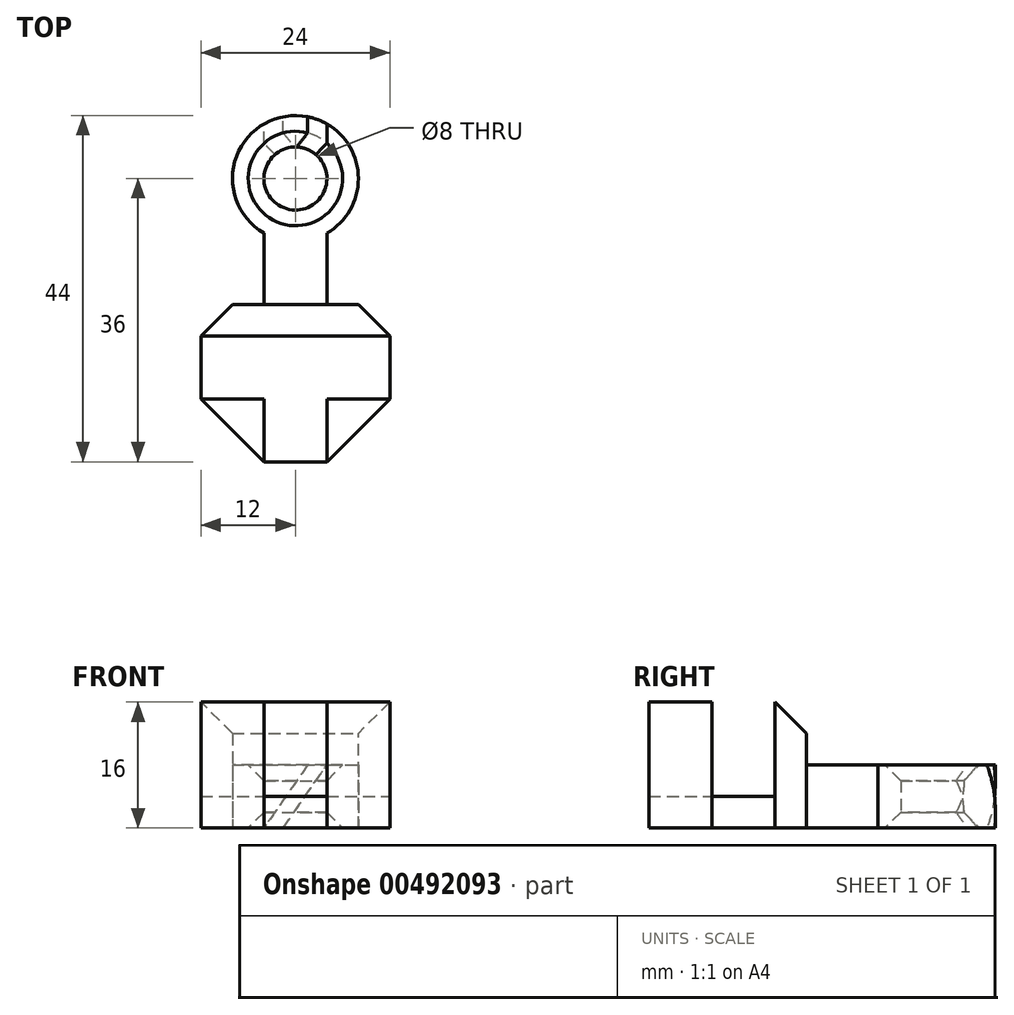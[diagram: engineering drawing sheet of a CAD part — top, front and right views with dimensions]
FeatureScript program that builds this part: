
annotation { "Feature Type Name" : "Feature", "Feature Type Description" : "" }
export const myFeature = defineFeature(function(context is Context, id is Id, definition is map)
    precondition{}
    {
        {
            var Q0;
            Q0=qCreatedBy(makeId("Top.planeOp"),FACE);
            var sketch = newSketch(context, id + "F0", { "sketchPlane" : qUnion([Q0])});
            skLineSegment(sketch, "E0.bottom", {"start": v(16, 4) * mm, "end": v(-16, 4) * mm});
            skLineSegment(sketch, "E0.top", {"start": v(16, -4) * mm, "end": v(-16, -4) * mm});
            skLineSegment(sketch, "E0.left", {"start": v(16, 4) * mm, "end": v(16, -4) * mm});
            skLineSegment(sketch, "E0.right", {"start": v(-16, 4) * mm, "end": v(-16, -4) * mm});
            skPoint(sketch, "E0.middle", {"position": v(0, 0) * mm});
            skLineSegment(sketch, "E1.bottom", {"start": v(-4, -4) * mm, "end": v(4, -4) * mm});
            skLineSegment(sketch, "E1.top", {"start": v(-4, -16) * mm, "end": v(4, -16) * mm});
            skLineSegment(sketch, "E1.left", {"start": v(-4, -4) * mm, "end": v(-4, -16) * mm});
            skLineSegment(sketch, "E1.right", {"start": v(4, -4) * mm, "end": v(4, -16) * mm});
            skLineSegment(sketch, "E2", {"start": v(-16, -4) * mm, "end": v(-16, -8) * mm});
            skLineSegment(sketch, "E3", {"start": v(-16, -8) * mm, "end": v(-8, -8) * mm});
            skLineSegment(sketch, "E4", {"start": v(-8, -8) * mm, "end": v(-8, -16) * mm});
            skLineSegment(sketch, "E5", {"start": v(-8, -16) * mm, "end": v(-4, -16) * mm});
            skLineSegment(sketch, "E6", {"start": v(-16, 4) * mm, "end": v(-16, 8) * mm});
            skLineSegment(sketch, "E7", {"start": v(-16, 8) * mm, "end": v(16, 8) * mm});
            skLineSegment(sketch, "E8", {"start": v(16, 8) * mm, "end": v(16, 4) * mm});
            skLineSegment(sketch, "E9", {"start": v(16, -4) * mm, "end": v(16, -8) * mm});
            skLineSegment(sketch, "E10", {"start": v(16, -8) * mm, "end": v(8, -8) * mm});
            skLineSegment(sketch, "E11", {"start": v(8, -8) * mm, "end": v(8, -16) * mm});
            skLineSegment(sketch, "E12", {"start": v(8, -16) * mm, "end": v(4, -16) * mm});
            skSolve(sketch);
        }
        {
            var Q0;
            Q0 = qSketchRegion(id + "F0", true);
            extrude(context, id + "F1", {"entities" : qUnion([Q0]), "depth" : 4 * mm});
        }
        {
            var Q0;
            {var subQ1=sQuery(id+"F0.wireOp",EDGE,"E1.left");Q0=makeQuery(id+"F0.imprint","IMPRINT",FACE,{"disambiguationData":[TD([[makeQuery(id+"F0.imprint","IMPRINT",EDGE,{"derivedFrom":subQ1}),-1.0]])]});}
            var Q1;
            {var subQ0=sQuery(id+"F0.wireOp",EDGE,"E1.right");Q1=makeQuery(id+"F0.imprint","IMPRINT",FACE,{"disambiguationData":[TD([[makeQuery(id+"F0.imprint","IMPRINT",EDGE,{"derivedFrom":subQ0}),1.0]])]});}
            var Q2;
            Q2=makeQuery(id+"F0.imprint","IMPRINT",FACE,{"disambiguationData":[TD([[makeQuery(id+"F0.imprint","IMPRINT",EDGE,{"derivedFrom":sQuery(id+"F0.wireOp",EDGE,"E0.bottom")}),-1.0]])]});
            extrude(context, id + "F2", {"entities" : qUnion([Q0, Q1, Q2]), "operationType" : NewBodyOperationType.ADD, "depth" : 16 * mm});
        }
        {
            var Q0;
            Q0=qCreatedBy(makeId("Top.planeOp"),FACE);
            var sketch = newSketch(context, id + "F3", { "sketchPlane" : qUnion([Q0])});
            skCircle(sketch, "E13", {"center": v(0, 24) * mm, "radius": 4 * mm});
            skCircle(sketch, "E14", {"center": v(0, 24) * mm, "radius": 8 * mm});
            skLineSegment(sketch, "E15.bottom", {"start": v(4, 17.07) * mm, "end": v(-4, 17.07) * mm, "construction": true});
            skLineSegment(sketch, "E15.top", {"start": v(4, 8) * mm, "end": v(-4, 8) * mm});
            skLineSegment(sketch, "E15.left", {"start": v(4, 17.07) * mm, "end": v(4, 8) * mm});
            skLineSegment(sketch, "E15.right", {"start": v(-4, 17.07) * mm, "end": v(-4, 8) * mm});
            skPoint(sketch, "E15.middle", {"position": v(0, 12.54) * mm});
            skPoint(sketch, "E16", {"position": v(0, 32) * mm});
            skSolve(sketch);
        }
        {
            var Q0;
            Q0=makeQuery(id+"F3.imprint","IMPRINT",FACE,{"disambiguationData":[TD([[makeQuery(id+"F3.imprint","IMPRINT",EDGE,{"derivedFrom":sQuery(id+"F3.wireOp",EDGE,"E15.top")}),-1.0]])]});
            var Q1;
            Q1=makeQuery(id+"F3.imprint","IMPRINT",FACE,{"disambiguationData":[TD([[makeQuery(id+"F3.imprint","IMPRINT",EDGE,{"derivedFrom":sQuery(id+"F3.wireOp",EDGE,"E13")}),-1.0]])]});
            var Q2;
            Q2=makeQuery(id+"F2.opExtrude","CAP_FACE",FACE,{"disambiguationData":[OSD([sQuery(id+"F0.wireOp",EDGE,"E0.bottom"),sQuery(id+"F0.wireOp",EDGE,"E6"),sQuery(id+"F0.wireOp",EDGE,"E7"),sQuery(id+"F0.wireOp",EDGE,"E8")])],"isStart":false});
            extrude(context, id + "F4", {"entities" : qUnion([Q0, Q1]), "operationType" : NewBodyOperationType.ADD, "endBoundEntityFace" : qUnion([Q2]), "offsetDistance" : 25 * mm, "depth" : 8 * mm});
        }
        {
            var Q0;
            {var subQ0=sQuery(id+"F0.wireOp",EDGE,"E7");Q0=makeQuery(id+"F2.boolean.opBoolean","MERGE",FACE,{"derivedFrom":[makeQuery(id+"F1.opExtrude","SWEPT_FACE",FACE,{"disambiguationData":[OSD([subQ0])]}),makeQuery(id+"F2.opExtrude","SWEPT_FACE",FACE,{"disambiguationData":[OSD([subQ0])]})]});}
            var Q1;
            Q1=sQuery(id+"F3.wireOp",VERTEX,"E16");
            cPlane(context, id + "F5", {"entities" : qUnion([Q0, Q1]), "cplaneType" : CPlaneType.PLANE_POINT, "offset" : 25 * mm, "width" : 150 * mm, "height" : 150 * mm});
        }
        {
            var Q0;
            Q0=qCreatedBy(id+"F5.planeOp",FACE);
            var sketch = newSketch(context, id + "F6", { "sketchPlane" : qUnion([Q0])});
            skLineSegment(sketch, "E17", {"start": v(-4, 8) * mm, "end": v(1.56, 0) * mm});
            skLineSegment(sketch, "E18", {"start": v(1.56, 0) * mm, "end": v(4, 0) * mm});
            skLineSegment(sketch, "E19", {"start": v(4, 0) * mm, "end": v(-1.56, 8) * mm});
            skLineSegment(sketch, "E20", {"start": v(-1.56, 8) * mm, "end": v(-4, 8) * mm});
            skLineSegment(sketch, "E21.0", {"start": v(-4, 8) * mm, "end": v(4, 8) * mm});
            skLineSegment(sketch, "E22.0", {"start": v(-4, 0) * mm, "end": v(4, 0) * mm});
            skSolve(sketch);
        }
        {
            var Q0;
            Q0 = qSketchRegion(id + "F6", true);
            extrude(context, id + "F7", {"entities" : qUnion([Q0]), "operationType" : NewBodyOperationType.REMOVE, "oppositeDirection" : true, "depth" : 8 * mm, "offsetDistance" : 25 * mm});
        }
        {
            var Q0;
            Q0=makeQuery(id+"F2.opExtrude","CAP_FACE",FACE,{"disambiguationData":[OSD([sQuery(id+"F0.wireOp",EDGE,"E0.top"),sQuery(id+"F0.wireOp",EDGE,"E1.right"),sQuery(id+"F0.wireOp",EDGE,"E9"),sQuery(id+"F0.wireOp",EDGE,"E10"),sQuery(id+"F0.wireOp",EDGE,"E11"),sQuery(id+"F0.wireOp",EDGE,"E12")])],"isStart":false});
            var sketch = newSketch(context, id + "F8", { "sketchPlane" : qUnion([Q0])});
            skLineSegment(sketch, "E23", {"start": v(-12, -4) * mm, "end": v(-4, -12) * mm});
            skLineSegment(sketch, "E24", {"start": v(-4, -12) * mm, "end": v(4, -12) * mm});
            skLineSegment(sketch, "E25", {"start": v(4, -12) * mm, "end": v(12, -4) * mm});
            skLineSegment(sketch, "E26", {"start": v(12, -4) * mm, "end": v(12, 4) * mm});
            skLineSegment(sketch, "E27", {"start": v(-12, -4) * mm, "end": v(-12, 4) * mm});
            skLineSegment(sketch, "E28", {"start": v(-12, 4) * mm, "end": v(-4, 12) * mm});
            skLineSegment(sketch, "E29", {"start": v(-4, 12) * mm, "end": v(4, 12) * mm, "construction": true});
            skLineSegment(sketch, "E30", {"start": v(4, 12) * mm, "end": v(12, 4) * mm});
            skLineSegment(sketch, "E31", {"start": v(-4, 12) * mm, "end": v(-21.85, 12) * mm});
            skLineSegment(sketch, "E32", {"start": v(-21.85, 12) * mm, "end": v(-21.85, -19.62) * mm});
            skLineSegment(sketch, "E33", {"start": v(-21.85, -19.62) * mm, "end": v(23.48, -19.62) * mm});
            skLineSegment(sketch, "E34", {"start": v(23.48, -19.62) * mm, "end": v(23.48, 12) * mm});
            skLineSegment(sketch, "E35", {"start": v(23.48, 12) * mm, "end": v(4, 12) * mm});
            skSolve(sketch);
        }
        {
            var Q0;
            {var subQ5=sQuery(id+"F8.wireOp",EDGE,"Dv1MXJR0-9d9j-Ba90-XDSw-6HdTQpo0Se9A");Q0=makeQuery(id+"F8.imprint","IMPRINT",FACE,{"disambiguationData":[TD([[makeQuery(id+"F8.imprint","IMPRINT",EDGE,{"derivedFrom":subQ5}),-1.0]])]});}
            var Q1;
            {var subQ1=makeQuery(id+"F2.opExtrude","CAP_EDGE",EDGE,{"disambiguationData":[OSD([sQuery(id+"F0.wireOp",EDGE,"E10")])],"isStart":false});Q1=makeQuery(id+"F8.imprint","IMPRINT",FACE,{"disambiguationData":[TD([[makeQuery(id+"F8.imprint","IMPRINT",EDGE,{"derivedFrom":subQ1}),1.0]])]});}
            var Q2;
            {var subQ1=makeQuery(id+"F2.opExtrude","CAP_EDGE",EDGE,{"disambiguationData":[OSD([sQuery(id+"F0.wireOp",EDGE,"E11")])],"isStart":false});Q2=makeQuery(id+"F8.imprint","IMPRINT",FACE,{"disambiguationData":[TD([[makeQuery(id+"F8.imprint","IMPRINT",EDGE,{"derivedFrom":subQ1}),-1.0]])]});}
            var Q3;
            {var subQ4=makeQuery(id+"F2.opExtrude","CAP_EDGE",EDGE,{"disambiguationData":[OSD([sQuery(id+"F0.wireOp",EDGE,"E10")])],"isStart":false});Q3=makeQuery(id+"F8.imprint","IMPRINT",FACE,{"disambiguationData":[TD([[makeQuery(id+"F8.imprint","IMPRINT",EDGE,{"derivedFrom":subQ4}),-1.0]])]});}
            var Q4;
            Q4=makeQuery(id+"F8.imprint","IMPRINT",FACE,{"disambiguationData":[TD([[makeQuery(id+"F8.imprint","IMPRINT",EDGE,{"derivedFrom":sQuery(id+"F8.wireOp",EDGE,"nhe9akcV-8vhA-wYRr-ZYu1-IHmTEResmYsJ")}),1.0]])]});
            var Q5;
            Q5=makeQuery(id+"F8.imprint","IMPRINT",FACE,{"disambiguationData":[TD([[makeQuery(id+"F8.imprint","IMPRINT",EDGE,{"derivedFrom":sQuery(id+"F8.wireOp",EDGE,"BqzB2uVe-haqs-R6YY-CTl4-DspGSjHFwzV3")}),-1.0]])]});
            extrude(context, id + "F9", {"entities" : qUnion([Q0, Q1, Q2, Q3, Q4, Q5]), "operationType" : NewBodyOperationType.REMOVE, "endBound" : BoundingType.THROUGH_ALL, "oppositeDirection" : true, "depth" : 25 * mm, "offsetDistance" : 25 * mm});
        }
        {
            var Q0;
            Q0=makeQuery(id+"F4.opExtrude","SWEPT_EDGE",EDGE,{"disambiguationData":[OSD([sQuery(id+"F3.wireOp",EDGE,"E15.top"),sQuery(id+"F3.wireOp",EDGE,"E15.right")])]});
            var Q1;
            Q1=makeQuery(id+"F4.opExtrude","SWEPT_EDGE",EDGE,{"disambiguationData":[OSD([sQuery(id+"F3.wireOp",EDGE,"E15.top"),sQuery(id+"F3.wireOp",EDGE,"E15.left")])]});
            var Q2;
            Q2=makeQuery(id+"F4.opExtrude","CAP_EDGE",EDGE,{"disambiguationData":[OSD([sQuery(id+"F3.wireOp",EDGE,"E15.top")])],"isStart":false});
            var Q3;
            Q3=makeQuery(id+"F2.opExtrude","CAP_EDGE",EDGE,{"disambiguationData":[OSD([sQuery(id+"F0.wireOp",EDGE,"E7")])],"isStart":false});
            chamfer(context, id + "F10", {"entities" : qUnion([Q0, Q1, Q2, Q3]), "width" : 4 * mm, "tangentPropagation" : true});
        }
        {
            var Q0;
            Q0=makeQuery(id+"F4.opExtrude","CAP_EDGE",EDGE,{"disambiguationData":[OSD([sQuery(id+"F3.wireOp",EDGE,"E13")])],"isStart":false});
            var Q1;
            Q1=makeQuery(id+"F4.opExtrude","CAP_EDGE",EDGE,{"disambiguationData":[OSD([sQuery(id+"F3.wireOp",EDGE,"E13")])],"isStart":true});
            chamfer(context, id + "F11", {"entities" : qUnion([Q0, Q1]), "width" : 2 * mm, "tangentPropagation" : true});
        }
    });
